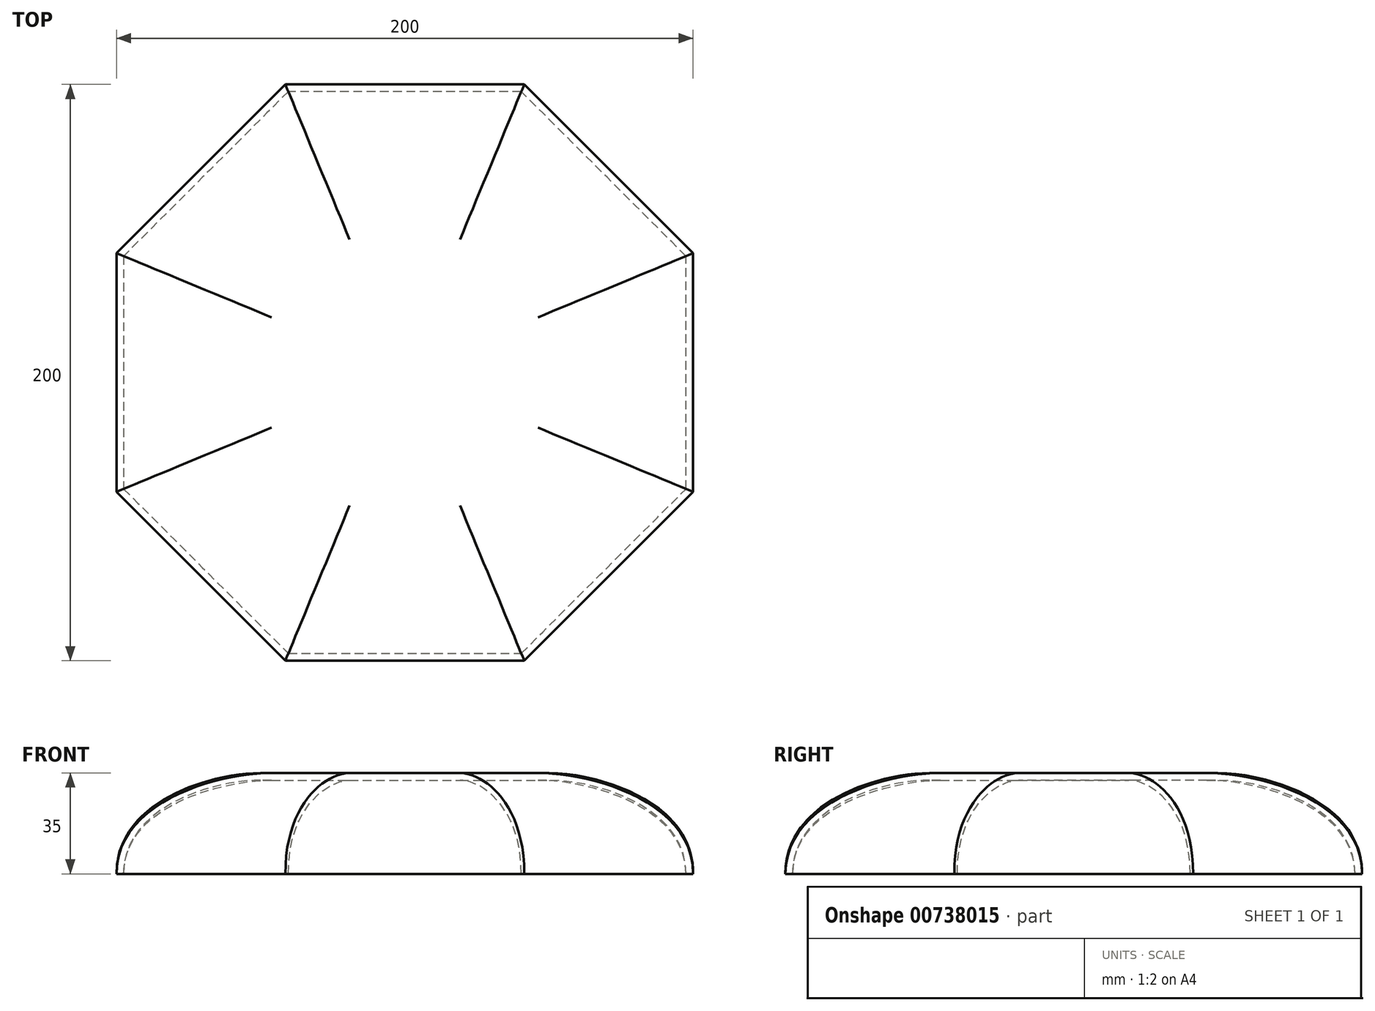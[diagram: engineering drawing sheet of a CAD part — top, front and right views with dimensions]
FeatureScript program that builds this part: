
annotation { "Feature Type Name" : "Feature", "Feature Type Description" : "" }
export const myFeature = defineFeature(function(context is Context, id is Id, definition is map)
    precondition{}
    {
        {
            var Q0;
            Q0=qCreatedBy(makeId("Top.planeOp"),FACE);
            var sketch = newSketch(context, id + "F0", { "sketchPlane" : qUnion([Q0])});
            skCircle(sketch, "E0.cCircle", {"center": v(0, 0) * mm, "radius": 100 * mm, "construction": true});
            skLineSegment(sketch, "E0.0", {"start": v(100, -41.42) * mm, "end": v(41.42, -100) * mm});
            skLineSegment(sketch, "E0.1", {"start": v(41.42, -100) * mm, "end": v(-41.42, -100) * mm});
            skLineSegment(sketch, "E0.2", {"start": v(-41.42, -100) * mm, "end": v(-100, -41.42) * mm});
            skLineSegment(sketch, "E0.3", {"start": v(-100, -41.42) * mm, "end": v(-100, 41.42) * mm});
            skLineSegment(sketch, "E0.4", {"start": v(-100, 41.42) * mm, "end": v(-41.42, 100) * mm});
            skLineSegment(sketch, "E0.5", {"start": v(-41.42, 100) * mm, "end": v(41.42, 100) * mm});
            skLineSegment(sketch, "E0.6", {"start": v(41.42, 100) * mm, "end": v(100, 41.42) * mm});
            skLineSegment(sketch, "E0.7", {"start": v(100, 41.42) * mm, "end": v(100, -41.42) * mm});
            skPoint(sketch, "E0.0.midPoint", {"position": v(70.71, -70.71) * mm});
            skSolve(sketch);
        }
        {
            var Q0;
            Q0=qCreatedBy(makeId("Top.planeOp"),FACE);
            cPlane(context, id + "F1", {"entities" : qUnion([Q0]), "cplaneType" : CPlaneType.OFFSET, "offset" : 35 * mm, "width" : 150 * mm, "height" : 150 * mm});
        }
        {
            var Q0;
            Q0=qCreatedBy(id+"F1.planeOp",FACE);
            var sketch = newSketch(context, id + "F2", { "sketchPlane" : qUnion([Q0])});
            skCircle(sketch, "E1", {"center": v(0, 0) * mm, "radius": 50 * mm});
            skPoint(sketch, "E2", {"position": v(19.13, 46.2) * mm});
            skLineSegment(sketch, "E3", {"start": v(0, 0) * mm, "end": v(41.42, 100) * mm, "construction": true});
            skPoint(sketch, "E4.1.0", {"position": v(-19.13, 46.2) * mm});
            skLineSegment(sketch, "E4.1.1", {"start": v(0, 0) * mm, "end": v(-41.42, 100) * mm, "construction": true});
            skPoint(sketch, "E4.2.0", {"position": v(-46.2, 19.13) * mm});
            skLineSegment(sketch, "E4.2.1", {"start": v(0, 0) * mm, "end": v(-100, 41.42) * mm, "construction": true});
            skPoint(sketch, "E4.3.0", {"position": v(-46.2, -19.13) * mm});
            skLineSegment(sketch, "E4.3.1", {"start": v(0, 0) * mm, "end": v(-100, -41.42) * mm, "construction": true});
            skPoint(sketch, "E4.4.0", {"position": v(-19.13, -46.2) * mm});
            skLineSegment(sketch, "E4.4.1", {"start": v(0, 0) * mm, "end": v(-41.42, -100) * mm, "construction": true});
            skPoint(sketch, "E4.5.0", {"position": v(19.13, -46.2) * mm});
            skLineSegment(sketch, "E4.5.1", {"start": v(0, 0) * mm, "end": v(41.42, -100) * mm, "construction": true});
            skPoint(sketch, "E4.6.0", {"position": v(46.2, -19.13) * mm});
            skLineSegment(sketch, "E4.6.1", {"start": v(0, 0) * mm, "end": v(100, -41.42) * mm, "construction": true});
            skPoint(sketch, "E4.7.0", {"position": v(46.2, 19.13) * mm});
            skLineSegment(sketch, "E4.7.1", {"start": v(0, 0) * mm, "end": v(100, 41.42) * mm, "construction": true});
            skSolve(sketch);
        }
        {
            var Q0;
            Q0=makeQuery(id+"F0.imprint","IMPRINT",FACE,{"disambiguationData":[TD([[makeQuery(id+"F0.imprint","IMPRINT",EDGE,{"derivedFrom":sQuery(id+"F0.wireOp",EDGE,"E0.0")}),-1.0]])]});
            var sketch = newSketch(context, id + "F3", { "sketchPlane" : qUnion([Q0])});
            skPoint(sketch, "E5", {"position": v(50, 0) * mm});
            skSolve(sketch);
        }
        {
            var Q0;
            Q0=sQuery(id+"F0.wireOp",VERTEX,"E0.7.end");
            var Q1;
            Q1=sQuery(id+"F2.wireOp",VERTEX,"E4.6.0");
            var Q2;
            Q2=sQuery(id+"F2.wireOp",VERTEX,"E1.center");
            cPlane(context, id + "F4", {"entities" : qUnion([Q0, Q1, Q2]), "cplaneType" : CPlaneType.THREE_POINT, "offset" : 25 * mm, "width" : 150 * mm, "height" : 150 * mm});
        }
        {
            var Q0;
            Q0=makeQuery(id+"F3.imprint","IMPRINT",FACE,{"disambiguationData":[TD([[makeQuery(id+"F3.imprint","IMPRINT",EDGE,{"derivedFrom":makeQuery(id+"F0.imprint","IMPRINT",EDGE,{"derivedFrom":sQuery(id+"F0.wireOp",EDGE,"E0.0")})}),-1.0]])]});
            var Q1;
            Q1=makeQuery(id+"F2.imprint","IMPRINT",FACE,{"disambiguationData":[TD([[makeQuery(id+"F2.imprint","IMPRINT",EDGE,{"derivedFrom":sQuery(id+"F2.wireOp",EDGE,"E1")}),1.0]])]});
            loft(context, id + "F5", {"startCondition" : LoftEndDerivativeType.NORMAL_TO_PROFILE, "startMagnitude" : 2, "endCondition" : LoftEndDerivativeType.TANGENT_TO_PROFILE, "endMagnitude" : 1, "sheetProfilesArray" : [{ "sheetProfileEntities" : qUnion([Q0]) }, { "sheetProfileEntities" : qUnion([Q1]) }]});
        }
        {
            var Q0;
            Q0=makeQuery(id+"F5.opLoft","CAP_FACE",FACE,{"disambiguationData":[OSD([makeQuery(id+"F3.imprint","IMPRINT",FACE,{"disambiguationData":[TD([[makeQuery(id+"F3.imprint","IMPRINT",EDGE,{"derivedFrom":makeQuery(id+"F0.imprint","IMPRINT",EDGE,{"derivedFrom":sQuery(id+"F0.wireOp",EDGE,"E0.0")})}),-1.0]])]})])],"isStart":true});
            shell(context, id + "F6", {"entities" : qUnion([Q0]), "thickness" : 2.5 * mm});
        }
    });
